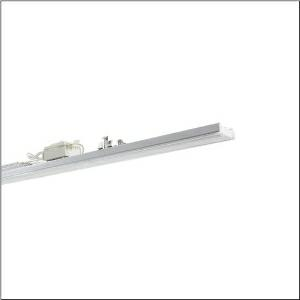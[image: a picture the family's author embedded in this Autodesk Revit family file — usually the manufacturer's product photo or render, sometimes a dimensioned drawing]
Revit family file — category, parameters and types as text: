
# Revit family: licross_21_recessed_mo_52tl1edn48xg
name_source: partatom
category: Lighting Fixtures
units: mm (PartAtom-declared; Revit-internal decimal feet)

## family parameters
Cut with Voids When Loaded = No
Host = Face
Light Source = No
Part Type = Normal
Room Calculation Point = No
Round Connector Dimension = Use Diameter
Shared = No

## types (1)
- --- (1 x LED, 8000 lm, 45.8 W, 4000K)
    Apparent Load = 46 VA
    CIE Flux Codes = 85 95 99 100 100
    Color Rendering = 80
    Color Temperature = 4000K
    Default Elevation = 1800 mm
    Description = Licross 21 Recessed MO, luminaire insert, of sheet steel, galvanised, coil coated, white, length: 1.500mm, width: 66mm, height: 67mm, LED rated luminous flux: 8.000lm, light colour: 840, SDCM (Standard Deviation of Colour Matching)MacAdam ≤ 3 SDCM (initial), control gear: DALI 2, with plug, 5-pole, with phase selection, mains connection: 220..240V, AC, 50/60Hz, rated input power: 46W, internal wiring halogen-free, primary light control with lens, of plastic, primary optical cover: cover, of PMMA, light emission: direct distribution, primary light characteristic: symmetric, protection rating (complete): IP40, insulation class (complete): insulation class I (protective earthing), certification: CE, ENEC, VDE, UKCA, protection symbol: D if used in an environment without relevant dust loads with corresponding accessories, impact resistance: IK06, permissible ambient temperature for indoor applications: -25..+40°C, corresponds to IFS (International Featured Standards) requirements for safety and quality in the food industry, reducing of maximum allowable ambient temperature of 5°C with ceiling mounting, LABS conformity tested according to VDMA 24364:2018-05, The light source and the operating device comply with the requirements of the Ecodesign Regulation (EU) 2019/2020 and are replaceable in accordance with this regulation, packaging unit: 1 piece
    Height = 58 mm
    Lamp = 1 x LED
    Lamp Light Flux = 8000 lm
    Lamp Power = 45.8 W
    Lamp count = 1
    Length = 1500 mm
    Luminous efficacy = 175 lm/W
    Manufacturer = Siteco
    ModVariant = No
    Model = 52TL1EDN48XG
    Mounting Place = Ceiling
    Mounting Type = Pendant
    Number of Poles = 1
    OnlyDefault = Yes
    Power Factor = 1
    Product Name = Licross 21 Recessed MO
    Product group = luminaire insert | ceiling pendant
    ProductGroupID = 901
    Protection Class = Protection class I
    Protection Degree = IP 40
    RLX_Detail_Level = 1
    RLX_Emergency_Light_Flux = 0 lm
    RLX_Emergency_Type = 0
    RLX_Emergency_Type_DB = No
    RlxData = <blob elided: 24973 chars, md5=ef4ddb68>
    Socket = socket
    Standby Power = 0 W
    System Light Flux = 8000 lm
    System Power = 46 W
    Type Comments = factory setting: luminous flux: 100 % | dim-lin: 254 | 308 mA
    Type Image = l_1296930.jpg
    URL = http://relux.com
    VarID = @adj_125429
    Voltage = 0 V
    Weight = 0.00 kg
    Width = 66 mm

## geometry (parser evidence)
native form markers: Blend x4, Sweep x11
no freeform markers — native parametric forms only
